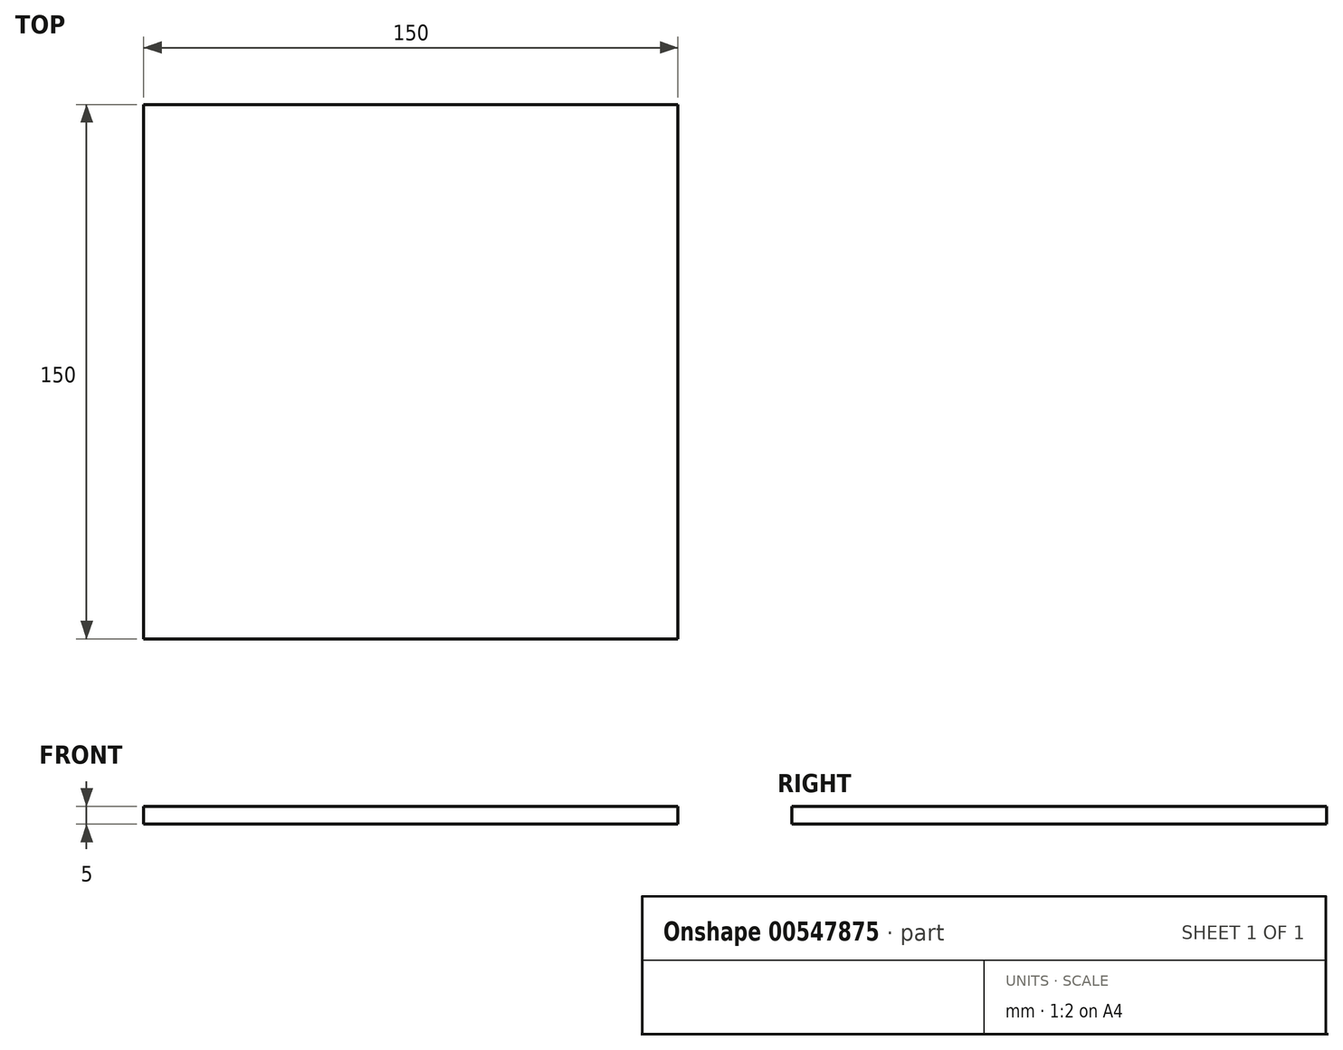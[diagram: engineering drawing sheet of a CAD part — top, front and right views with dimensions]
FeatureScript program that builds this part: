
annotation { "Feature Type Name" : "Feature", "Feature Type Description" : "" }
export const myFeature = defineFeature(function(context is Context, id is Id, definition is map)
    precondition{}
    {
        {
            var Q0;
            Q0=qCreatedBy(makeId("Top.planeOp"),FACE);
            var sketch = newSketch(context, id + "F0", { "sketchPlane" : qUnion([Q0])});
            skLineSegment(sketch, "E0.bottom", {"start": v(-78.94, 72.98) * mm, "end": v(71.06, 72.98) * mm});
            skLineSegment(sketch, "E0.top", {"start": v(-78.94, -77.02) * mm, "end": v(71.06, -77.02) * mm});
            skLineSegment(sketch, "E0.left", {"start": v(-78.94, 72.98) * mm, "end": v(-78.94, -77.02) * mm});
            skLineSegment(sketch, "E0.right", {"start": v(71.06, 72.98) * mm, "end": v(71.06, -77.02) * mm});
            skSolve(sketch);
        }
        {
            var Q0;
            Q0=makeQuery(id+"F0.imprint","IMPRINT",FACE,{"disambiguationData":[TD([[makeQuery(id+"F0.imprint","IMPRINT",EDGE,{"derivedFrom":sQuery(id+"F0.wireOp",EDGE,"E0.bottom")}),-1.0]])]});
            extrude(context, id + "F1", {"entities" : qUnion([Q0]), "depth" : 5 * mm, "offsetDistance" : 25 * mm});
        }
    });
